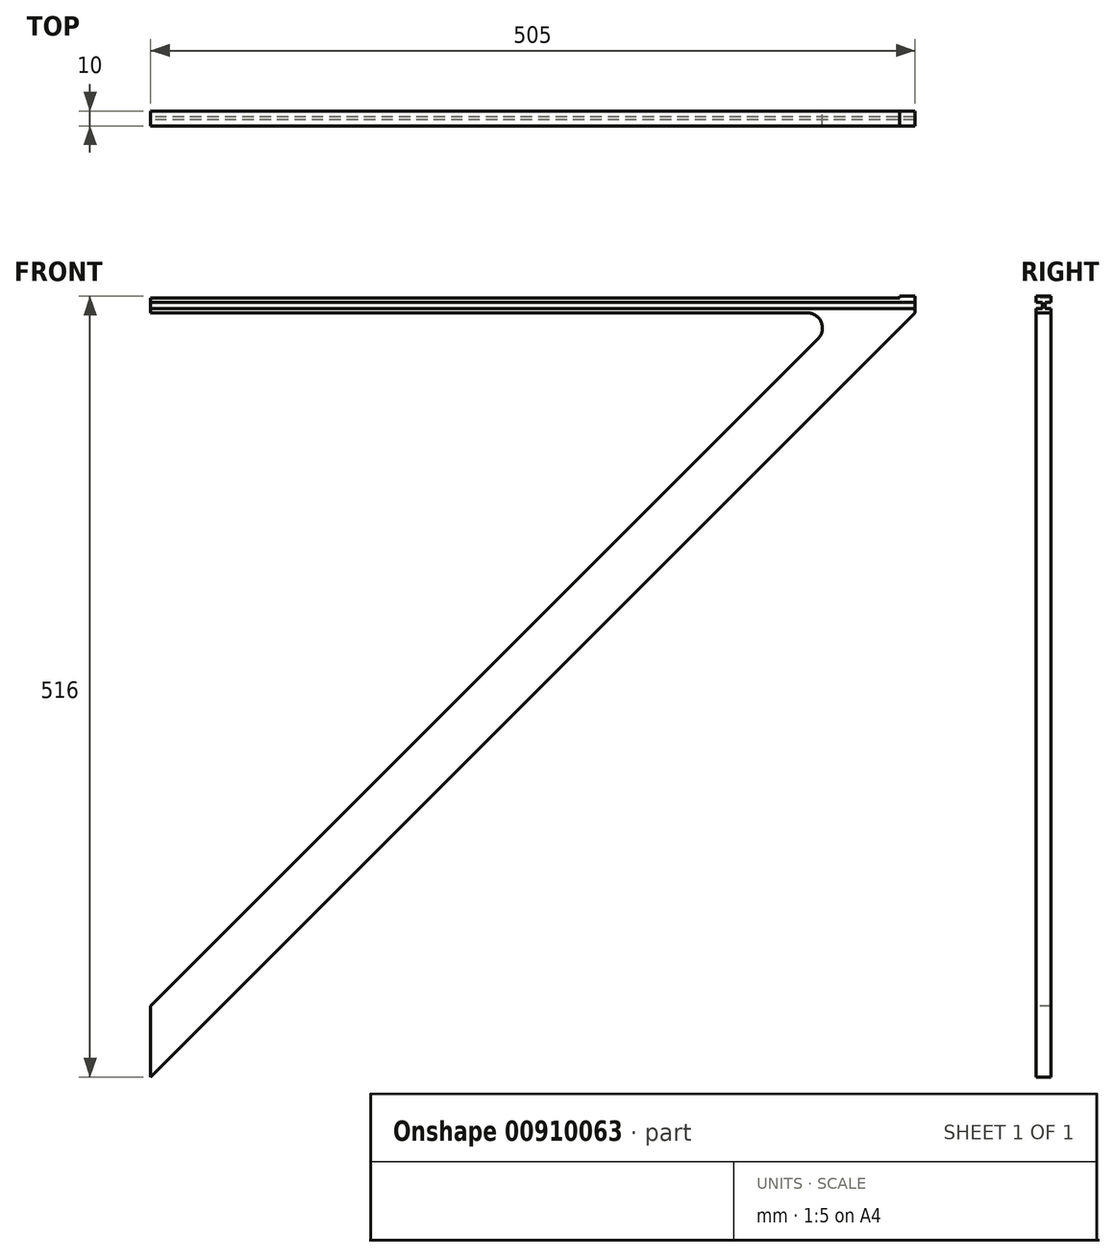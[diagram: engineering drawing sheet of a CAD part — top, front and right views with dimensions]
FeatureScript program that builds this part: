
annotation { "Feature Type Name" : "Feature", "Feature Type Description" : "" }
export const myFeature = defineFeature(function(context is Context, id is Id, definition is map)
    precondition{}
    {
        {
            var Q0;
            Q0=qCreatedBy(makeId("Right.planeOp"),FACE);
            var sketch = newSketch(context, id + "F0", { "sketchPlane" : qUnion([Q0])});
            skLineSegment(sketch, "E0", {"start": v(0, 0) * mm, "end": v(-1, 0) * mm});
            skLineSegment(sketch, "E1", {"start": v(-1, 0) * mm, "end": v(-1, 2) * mm});
            skLineSegment(sketch, "E2", {"start": v(-1, 2) * mm, "end": v(-5, 2) * mm});
            skLineSegment(sketch, "E3", {"start": v(-5, 2) * mm, "end": v(-5, 5) * mm});
            skLineSegment(sketch, "E4", {"start": v(-5, 5) * mm, "end": v(0, 5) * mm});
            skLineSegment(sketch, "E5.MirrorCS", {"start": v(5, 5) * mm, "end": v(0, 5) * mm});
            skLineSegment(sketch, "E6.MirrorCS", {"start": v(5, 2) * mm, "end": v(5, 5) * mm});
            skLineSegment(sketch, "E7.MirrorCS", {"start": v(1, 2) * mm, "end": v(5, 2) * mm});
            skLineSegment(sketch, "E8.MirrorCS", {"start": v(1, 0) * mm, "end": v(1, 2) * mm});
            skLineSegment(sketch, "E9.MirrorCS", {"start": v(-1, 0) * mm, "end": v(-1, -2) * mm});
            skLineSegment(sketch, "E10.MirrorCS", {"start": v(1, 0) * mm, "end": v(1, -2) * mm});
            skLineSegment(sketch, "E11.MirrorCS", {"start": v(-1, -2) * mm, "end": v(-5, -2) * mm});
            skLineSegment(sketch, "E12.MirrorCS", {"start": v(1, -2) * mm, "end": v(5, -2) * mm});
            skLineSegment(sketch, "E13.MirrorCS", {"start": v(-5, -2) * mm, "end": v(-5, -5) * mm});
            skLineSegment(sketch, "E14.MirrorCS", {"start": v(5, -2) * mm, "end": v(5, -5) * mm});
            skLineSegment(sketch, "E15.MirrorCS", {"start": v(5, -5) * mm, "end": v(0, -5) * mm});
            skLineSegment(sketch, "E16.MirrorCS", {"start": v(-5, -5) * mm, "end": v(0, -5) * mm});
            skSolve(sketch);
        }
        {
            var Q0;
            Q0 = qSketchRegion(id + "F0", true);
            extrude(context, id + "F1", {"entities" : qUnion([Q0]), "depth" : 505 * mm, "offsetDistance" : 25 * mm});
        }
        {
            var Q0;
            Q0=makeQuery(id+"F1.opExtrude","SWEPT_FACE",FACE,{"disambiguationData":[OSD([sQuery(id+"F0.wireOp",EDGE,"E4"),sQuery(id+"F0.wireOp",EDGE,"E5.MirrorCS")])]});
            var sketch = newSketch(context, id + "F2", { "sketchPlane" : qUnion([Q0])});
            skLineSegment(sketch, "E17", {"start": v(505, 5) * mm, "end": v(495, 5) * mm});
            skLineSegment(sketch, "E18", {"start": v(495, 5) * mm, "end": v(495, -5) * mm});
            skLineSegment(sketch, "E19", {"start": v(505, -5) * mm, "end": v(495, -5) * mm});
            skLineSegment(sketch, "E20", {"start": v(505, 5) * mm, "end": v(505, -5) * mm});
            skSolve(sketch);
        }
        {
            var Q0;
            Q0 = qSketchRegion(id + "F2", true);
            extrude(context, id + "F3", {"entities" : qUnion([Q0]), "operationType" : NewBodyOperationType.ADD, "depth" : 1 * mm, "offsetDistance" : 25 * mm});
        }
        {
            var Q0;
            Q0=makeQuery(id+"F1.opExtrude","SWEPT_FACE",FACE,{"disambiguationData":[OSD([sQuery(id+"F0.wireOp",EDGE,"E15.MirrorCS"),sQuery(id+"F0.wireOp",EDGE,"E16.MirrorCS")])]});
            var sketch = newSketch(context, id + "F4", { "sketchPlane" : qUnion([Q0])});
            skLineSegment(sketch, "E21", {"start": v(0, 5) * mm, "end": v(0, -5) * mm});
            skLineSegment(sketch, "E22", {"start": v(0, -5) * mm, "end": v(505, -5) * mm});
            skLineSegment(sketch, "E23", {"start": v(505, -5) * mm, "end": v(505, 5) * mm});
            skLineSegment(sketch, "E24", {"start": v(505, 5) * mm, "end": v(0, 5) * mm});
            skSolve(sketch);
        }
        {
            var Q0;
            Q0 = qSketchRegion(id + "F4", true);
            extrude(context, id + "F5", {"entities" : qUnion([Q0]), "operationType" : NewBodyOperationType.ADD, "depth" : 505 * mm, "offsetDistance" : 25 * mm});
        }
        {
            var Q0;
            Q0=makeQuery(id+"F5.boolean.opBoolean","MERGE",FACE,{"derivedFrom":[makeQuery(id+"F1.opExtrude","SWEPT_FACE",FACE,{"disambiguationData":[OSD([sQuery(id+"F0.wireOp",EDGE,"E13.MirrorCS")])]}),makeQuery(id+"F5.opExtrude","SWEPT_FACE",FACE,{"disambiguationData":[OSD([sQuery(id+"F4.wireOp",EDGE,"E24")])]})]});
            var sketch = newSketch(context, id + "F6", { "sketchPlane" : qUnion([Q0])});
            skLineSegment(sketch, "E25", {"start": v(0, -510) * mm, "end": v(0, -463) * mm});
            skLineSegment(sketch, "E26", {"start": v(0, -463) * mm, "end": v(0, -5) * mm});
            skLineSegment(sketch, "E27", {"start": v(0, -5) * mm, "end": v(458, -5) * mm});
            skLineSegment(sketch, "E28", {"start": v(458, -5) * mm, "end": v(0, -463) * mm});
            skSolve(sketch);
        }
        {
            var Q0;
            Q0 = qSketchRegion(id + "F6", true);
            extrude(context, id + "F7", {"entities" : qUnion([Q0]), "operationType" : NewBodyOperationType.REMOVE, "endBound" : BoundingType.THROUGH_ALL, "oppositeDirection" : true, "depth" : 25 * mm, "offsetDistance" : 25 * mm});
        }
        {
            var Q0;
            Q0 = qSketchRegion(id + "F6", true);
            extrude(context, id + "F8", {"entities" : qUnion([Q0]), "operationType" : NewBodyOperationType.REMOVE, "endBound" : BoundingType.THROUGH_ALL, "oppositeDirection" : true, "depth" : 25 * mm, "offsetDistance" : 25 * mm});
        }
        {
            var Q0;
            Q0=makeQuery(id+"F5.boolean.opBoolean","MERGE",FACE,{"derivedFrom":[makeQuery(id+"F1.opExtrude","SWEPT_FACE",FACE,{"disambiguationData":[OSD([sQuery(id+"F0.wireOp",EDGE,"E13.MirrorCS")])]}),makeQuery(id+"F5.opExtrude","SWEPT_FACE",FACE,{"disambiguationData":[OSD([sQuery(id+"F4.wireOp",EDGE,"E24")])]})]});
            var sketch = newSketch(context, id + "F9", { "sketchPlane" : qUnion([Q0])});
            skLineSegment(sketch, "E29", {"start": v(0, -510) * mm, "end": v(505, -510) * mm});
            skLineSegment(sketch, "E30", {"start": v(505, -510) * mm, "end": v(505, -5) * mm});
            skLineSegment(sketch, "E31", {"start": v(0, -510) * mm, "end": v(505, -5) * mm});
            skSolve(sketch);
        }
        {
            var Q0;
            Q0 = qSketchRegion(id + "F9", true);
            extrude(context, id + "F10", {"entities" : qUnion([Q0]), "operationType" : NewBodyOperationType.REMOVE, "endBound" : BoundingType.THROUGH_ALL, "oppositeDirection" : true, "depth" : 25 * mm, "offsetDistance" : 25 * mm});
        }
        {
            var Q0;
            Q0=makeQuery(id+"F7.boolean.opBoolean","COPY",EDGE,{"derivedFrom":makeQuery(id+"F7.opExtrude","SWEPT_EDGE",EDGE,{"disambiguationData":[OSD([sQuery(id+"F6.wireOp",EDGE,"E27"),sQuery(id+"F6.wireOp",EDGE,"E28")])]})});
            fillet(context, id + "F11", {"entities" : qUnion([Q0]), "radius" : 10 * mm, "tangentPropagation" : true, "allowEdgeOverflow" : false});
        }
    });
